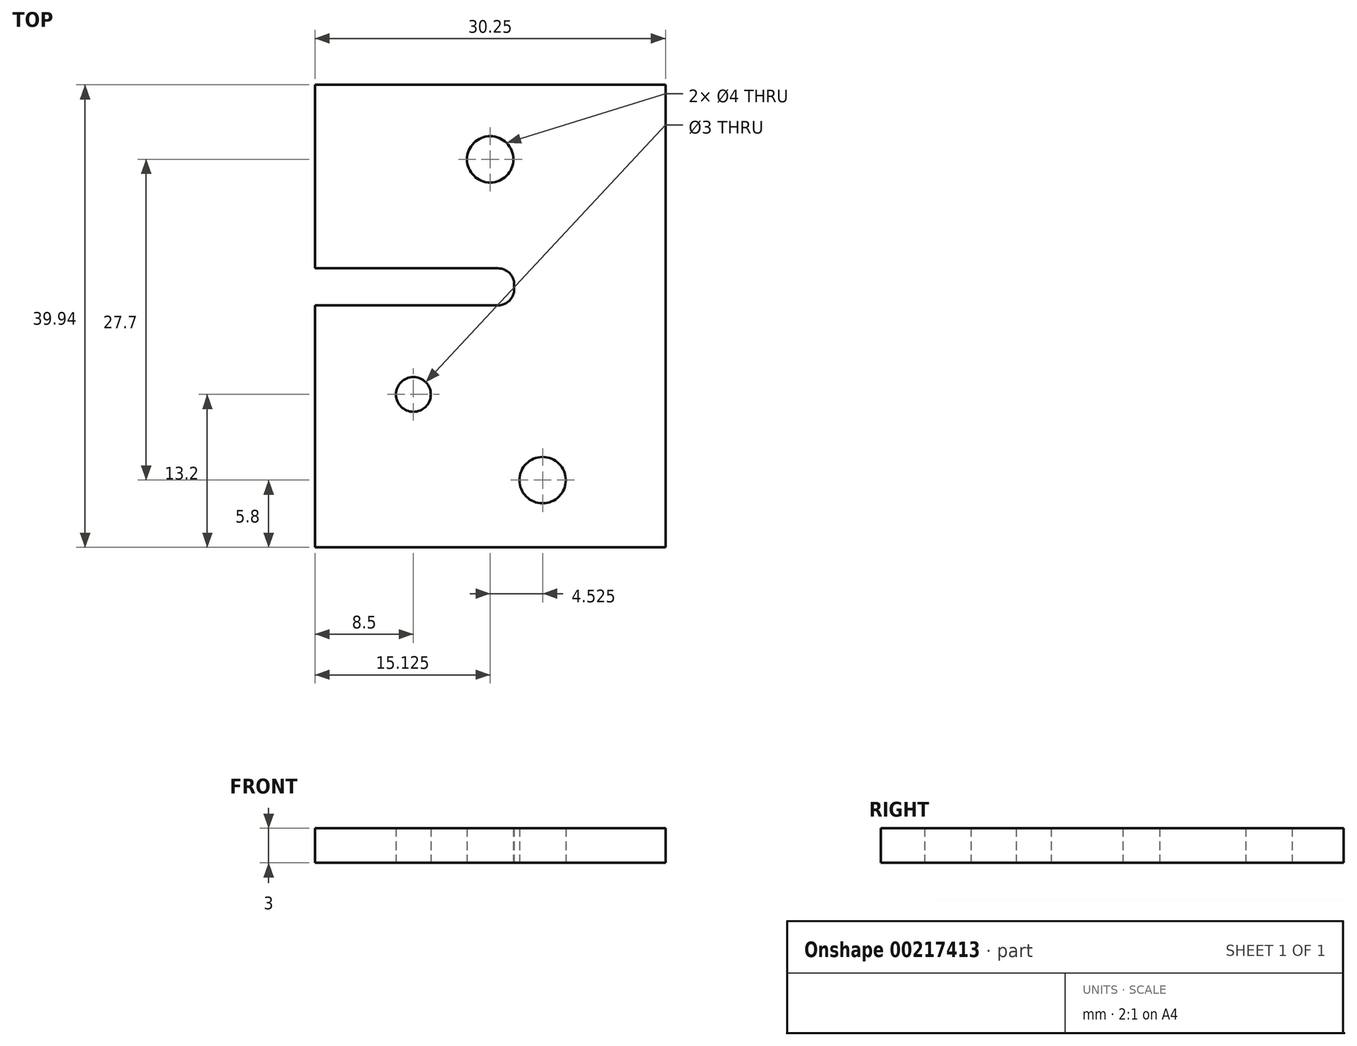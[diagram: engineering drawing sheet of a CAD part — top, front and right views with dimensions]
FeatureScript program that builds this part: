
annotation { "Feature Type Name" : "Feature", "Feature Type Description" : "" }
export const myFeature = defineFeature(function(context is Context, id is Id, definition is map)
    precondition{}
    {
        {
            var Q0;
            Q0=qCreatedBy(makeId("Top.planeOp"),FACE);
            var sketch = newSketch(context, id + "F0", { "sketchPlane" : qUnion([Q0])});
            skLineSegment(sketch, "E0.bottom", {"start": v(0, 0) * mm, "end": v(30.25, 0) * mm});
            skLineSegment(sketch, "E0.left", {"start": v(0, 0) * mm, "end": v(0, 20.9) * mm});
            skLineSegment(sketch, "E0.right", {"start": v(30.25, 0) * mm, "end": v(30.25, 24.1) * mm});
            skLineSegment(sketch, "E1.top", {"start": v(0, 24.1) * mm, "end": v(15.8, 24.1) * mm});
            skLineSegment(sketch, "E1.left", {"start": v(0, 39.94) * mm, "end": v(0, 24.1) * mm});
            skLineSegment(sketch, "E1.right", {"start": v(30.25, 39.94) * mm, "end": v(30.25, 24.1) * mm});
            skLineSegment(sketch, "E2", {"start": v(0, 20.9) * mm, "end": v(15.8, 20.9) * mm});
            skLineSegment(sketch, "E3", {"start": v(17.2, 22.7) * mm, "end": v(17.2, 22.3) * mm});
            skLineSegment(sketch, "E4.trimOffspring", {"start": v(0, 24.1) * mm, "end": v(0, 39.94) * mm});
            skCircle(sketch, "E5", {"center": v(15.12, 33.5) * mm, "radius": 2 * mm});
            skLineSegment(sketch, "E6", {"start": v(0, 39.94) * mm, "end": v(30.25, 39.94) * mm});
            skPoint(sketch, "E7.visualSharp", {"position": v(17.2, 24.1) * mm});
            skArc(sketch, "E7.filletArc", {"start": v(17.2, 22.7) * mm, "mid": v(16.79, 23.68) * mm, "end": v(15.8, 24.1) * mm});
            skPoint(sketch, "E8.visualSharp", {"position": v(17.2, 20.9) * mm});
            skArc(sketch, "E8.filletArc", {"start": v(15.8, 20.9) * mm, "mid": v(16.79, 21.31) * mm, "end": v(17.2, 22.3) * mm});
            skCircle(sketch, "E9", {"center": v(8.5, 13.2) * mm, "radius": 1.5 * mm});
            skCircle(sketch, "E10", {"center": v(19.65, 5.8) * mm, "radius": 2 * mm});
            skSolve(sketch);
        }
        {
            var Q0;
            Q0=makeQuery(id+"F0.imprint","IMPRINT",FACE,{"disambiguationData":[TD([[makeQuery(id+"F0.imprint","IMPRINT",EDGE,{"derivedFrom":sQuery(id+"F0.wireOp",EDGE,"E0.bottom")}),1.0]])]});
            extrude(context, id + "F1", {"entities" : qUnion([Q0]), "depth" : 3 * mm});
        }
    });
